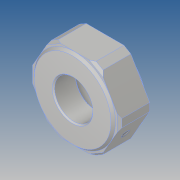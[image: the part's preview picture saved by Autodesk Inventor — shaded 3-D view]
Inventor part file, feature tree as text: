
AUTODESK INVENTOR PART (.ipt)
format: ipt  version: 2019 (Build 230136000, 136)  size: 201,216 bytes
history: native  units: mm
features: chamfer x4, other x2, sketch x2, extrude x1, hole x1, pattern_circular x1
ambient origin geometry x8: Origin, YZ Plane, XZ Plane, XY Plane, X Axis, Y Axis, Z Axis, Center Point
bodies: Solide1 (feature_tree)
feature tree (11):
  other  "Révolution1"
  other  "Plan de construction1"
  extrude  "Extrusion1"  Depth=16.5mm
  chamfer  "Chanfrein1"  Distance=22.0mm
  chamfer  "Chanfrein2"  Distance=35.0mm
  hole  "Perçage1"  [1 undecoded]
  chamfer  "Chanfrein4"  Angle=90.0deg  [1 undecoded]
  chamfer  "Chanfrein5"  Distance=13.0mm
  pattern_circular  "Réseau circulaire2"  Angle=45.0deg  [1 undecoded]
  sketch  "Esquisse1"
  sketch  "Esquisse2"
note: 3 required parameter values undecoded (feature->parameter linkage not recoverable at this tier; creation-order binding heuristic only, values carry confidence <= 0.55)
